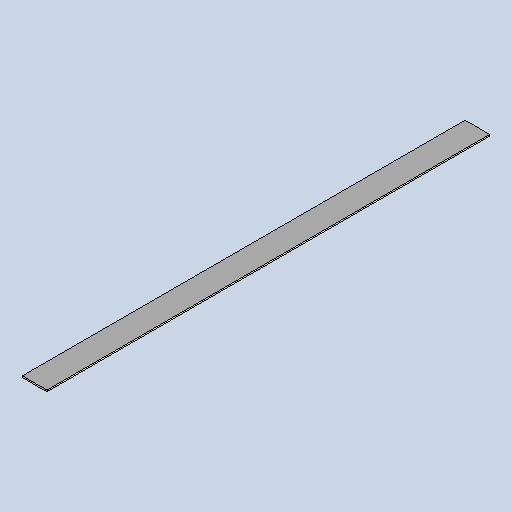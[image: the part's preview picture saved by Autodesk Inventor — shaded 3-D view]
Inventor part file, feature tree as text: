
AUTODESK INVENTOR PART (.ipt)
format: ipt  version: 2025 (Build 290162010, 162A)  size: 261,632 bytes
history: native  units: mm
features: sheet_metal_op x1, sketch x1, other x1
ambient origin geometry x8: Origin, YZ Plane, XZ Plane, XY Plane, X Axis, Y Axis, Z Axis, Center Point
bodies: Body1 (feature_tree)
feature tree (3):
  sheet_metal_op  "Face2"
  sketch  "Sketch1"  dims[d11=1100.0mm d12=900.0mm d13=25.0mm d14=25.0mm d15=3.0mm]
  other  "Plate2"
